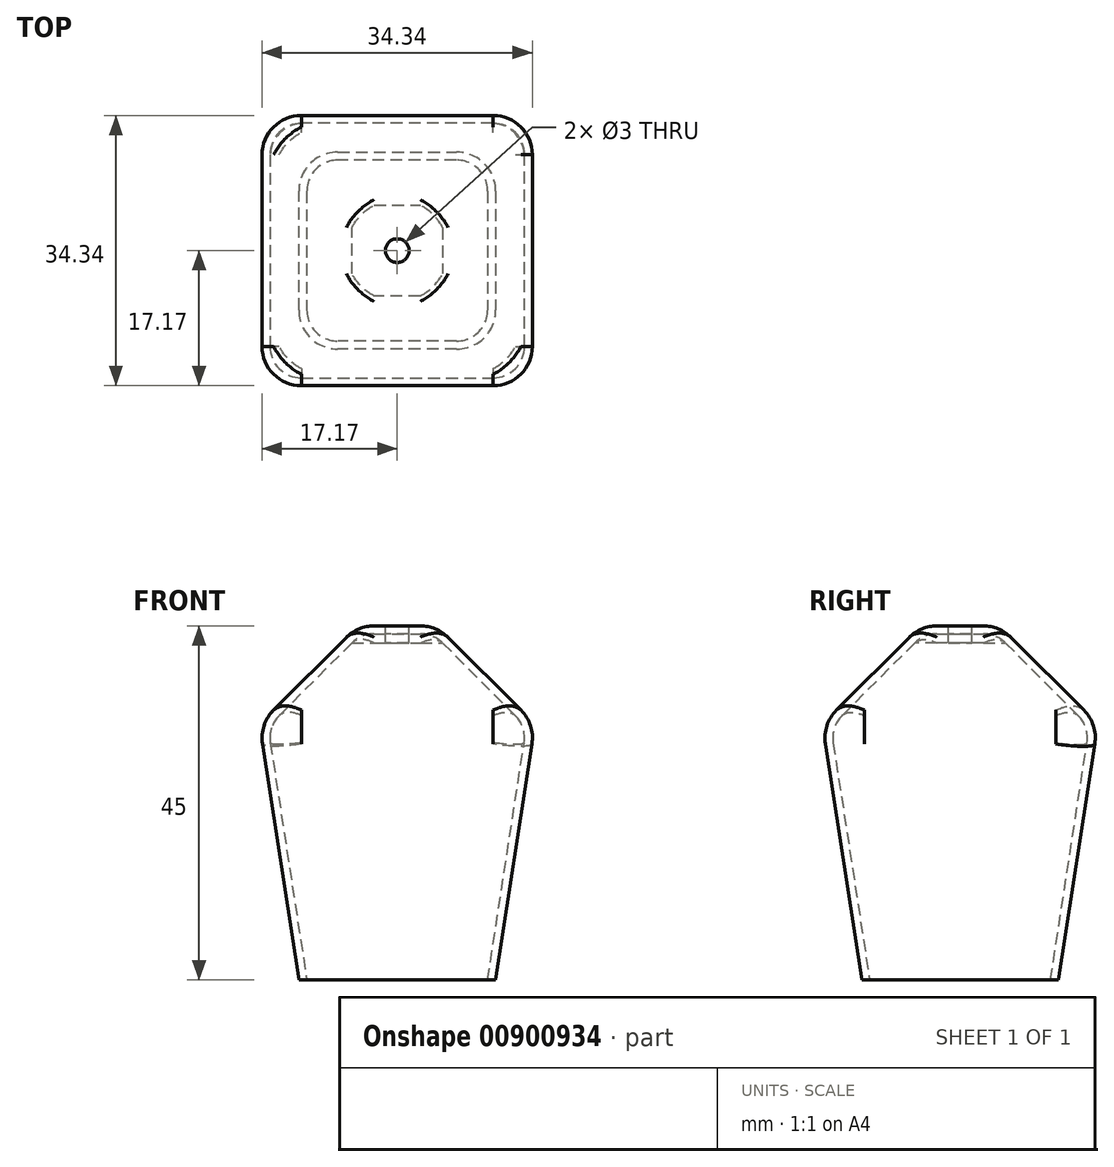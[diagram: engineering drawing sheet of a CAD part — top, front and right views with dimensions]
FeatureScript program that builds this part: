
annotation { "Feature Type Name" : "Feature", "Feature Type Description" : "" }
export const myFeature = defineFeature(function(context is Context, id is Id, definition is map)
    precondition{}
    {
        {
            var Q0;
            Q0=qCreatedBy(makeId("Top.planeOp"),FACE);
            var sketch = newSketch(context, id + "F0", { "sketchPlane" : qUnion([Q0])});
            skLineSegment(sketch, "E0.bottom", {"start": v(17.5, 17.5) * mm, "end": v(-17.5, 17.5) * mm});
            skLineSegment(sketch, "E0.top", {"start": v(17.5, -17.5) * mm, "end": v(-17.5, -17.5) * mm});
            skLineSegment(sketch, "E0.left", {"start": v(17.5, 17.5) * mm, "end": v(17.5, -17.5) * mm});
            skLineSegment(sketch, "E0.right", {"start": v(-17.5, 17.5) * mm, "end": v(-17.5, -17.5) * mm});
            skPoint(sketch, "E0.middle", {"position": v(0, 0) * mm});
            skSolve(sketch);
        }
        {
            var Q0;
            Q0 = qSketchRegion(id + "F0", true);
            extrude(context, id + "F1", {"entities" : qUnion([Q0]), "depth" : 45 * mm, "offsetDistance" : 25 * mm});
        }
        {
            var Q0;
            Q0=makeQuery(id+"F1.opExtrude","CAP_EDGE",EDGE,{"disambiguationData":[OSD([sQuery(id+"F0.wireOp",EDGE,"E0.left")])],"isStart":false});
            var Q1;
            Q1=makeQuery(id+"F1.opExtrude","CAP_EDGE",EDGE,{"disambiguationData":[OSD([sQuery(id+"F0.wireOp",EDGE,"E0.top")])],"isStart":false});
            var Q2;
            Q2=makeQuery(id+"F1.opExtrude","CAP_EDGE",EDGE,{"disambiguationData":[OSD([sQuery(id+"F0.wireOp",EDGE,"E0.right")])],"isStart":false});
            var Q3;
            Q3=makeQuery(id+"F1.opExtrude","CAP_EDGE",EDGE,{"disambiguationData":[OSD([sQuery(id+"F0.wireOp",EDGE,"E0.bottom")])],"isStart":false});
            chamfer(context, id + "F2", {"entities" : qUnion([Q0, Q1, Q2, Q3]), "width" : 12.5 * mm, "tangentPropagation" : true});
        }
        {
            var Q0;
            Q0=makeQuery(id+"F1.opExtrude","CAP_EDGE",EDGE,{"disambiguationData":[OSD([sQuery(id+"F0.wireOp",EDGE,"E0.left")])],"isStart":true});
            var Q1;
            Q1=makeQuery(id+"F1.opExtrude","CAP_EDGE",EDGE,{"disambiguationData":[OSD([sQuery(id+"F0.wireOp",EDGE,"E0.top")])],"isStart":true});
            var Q2;
            Q2=makeQuery(id+"F1.opExtrude","CAP_EDGE",EDGE,{"disambiguationData":[OSD([sQuery(id+"F0.wireOp",EDGE,"E0.right")])],"isStart":true});
            var Q3;
            Q3=makeQuery(id+"F1.opExtrude","CAP_EDGE",EDGE,{"disambiguationData":[OSD([sQuery(id+"F0.wireOp",EDGE,"E0.bottom")])],"isStart":true});
            chamfer(context, id + "F3", {"entities" : qUnion([Q0, Q1, Q2, Q3]), "chamferType" : ChamferType.TWO_OFFSETS, "width1" : 32.5 * mm, "oppositeDirection" : true, "width2" : 5 * mm, "tangentPropagation" : true});
        }
        {
            var Q0;
            {var subQ0=sQuery(id+"F0.wireOp",EDGE,"E0.top");Q0=makeQuery(id+"F2.opChamfer","BLEND_EDGE",EDGE,{"blendedFrom":[makeQuery(id+"F1.opExtrude","CAP_EDGE",EDGE,{"disambiguationData":[OSD([subQ0])],"isStart":false}),makeQuery(id+"F1.opExtrude","CAP_FACE",FACE,{"disambiguationData":[OSD([sQuery(id+"F0.wireOp",EDGE,"E0.bottom"),subQ0,sQuery(id+"F0.wireOp",EDGE,"E0.left"),sQuery(id+"F0.wireOp",EDGE,"E0.right")])],"isStart":false})],"blendedInto":[makeQuery(id+"F1.opExtrude","CAP_FACE",FACE,{"disambiguationData":[OSD([sQuery(id+"F0.wireOp",EDGE,"E0.bottom"),subQ0,sQuery(id+"F0.wireOp",EDGE,"E0.left"),sQuery(id+"F0.wireOp",EDGE,"E0.right")])],"isStart":false})]});}
            var Q1;
            {var subQ0=sQuery(id+"F0.wireOp",EDGE,"E0.left");Q1=makeQuery(id+"F2.opChamfer","BLEND_EDGE",EDGE,{"blendedFrom":[makeQuery(id+"F1.opExtrude","CAP_EDGE",EDGE,{"disambiguationData":[OSD([subQ0])],"isStart":false}),makeQuery(id+"F1.opExtrude","CAP_FACE",FACE,{"disambiguationData":[OSD([sQuery(id+"F0.wireOp",EDGE,"E0.bottom"),sQuery(id+"F0.wireOp",EDGE,"E0.top"),subQ0,sQuery(id+"F0.wireOp",EDGE,"E0.right")])],"isStart":false})],"blendedInto":[makeQuery(id+"F1.opExtrude","CAP_FACE",FACE,{"disambiguationData":[OSD([sQuery(id+"F0.wireOp",EDGE,"E0.bottom"),sQuery(id+"F0.wireOp",EDGE,"E0.top"),subQ0,sQuery(id+"F0.wireOp",EDGE,"E0.right")])],"isStart":false})]});}
            var Q2;
            {var subQ0=sQuery(id+"F0.wireOp",EDGE,"E0.bottom");Q2=makeQuery(id+"F2.opChamfer","BLEND_EDGE",EDGE,{"blendedFrom":[makeQuery(id+"F1.opExtrude","CAP_EDGE",EDGE,{"disambiguationData":[OSD([subQ0])],"isStart":false}),makeQuery(id+"F1.opExtrude","CAP_FACE",FACE,{"disambiguationData":[OSD([subQ0,sQuery(id+"F0.wireOp",EDGE,"E0.top"),sQuery(id+"F0.wireOp",EDGE,"E0.left"),sQuery(id+"F0.wireOp",EDGE,"E0.right")])],"isStart":false})],"blendedInto":[makeQuery(id+"F1.opExtrude","CAP_FACE",FACE,{"disambiguationData":[OSD([subQ0,sQuery(id+"F0.wireOp",EDGE,"E0.top"),sQuery(id+"F0.wireOp",EDGE,"E0.left"),sQuery(id+"F0.wireOp",EDGE,"E0.right")])],"isStart":false})]});}
            var Q3;
            {var subQ0=sQuery(id+"F0.wireOp",EDGE,"E0.right");Q3=makeQuery(id+"F2.opChamfer","BLEND_EDGE",EDGE,{"blendedFrom":[makeQuery(id+"F1.opExtrude","CAP_EDGE",EDGE,{"disambiguationData":[OSD([subQ0])],"isStart":false}),makeQuery(id+"F1.opExtrude","CAP_FACE",FACE,{"disambiguationData":[OSD([sQuery(id+"F0.wireOp",EDGE,"E0.bottom"),sQuery(id+"F0.wireOp",EDGE,"E0.top"),sQuery(id+"F0.wireOp",EDGE,"E0.left"),subQ0])],"isStart":false})],"blendedInto":[makeQuery(id+"F1.opExtrude","CAP_FACE",FACE,{"disambiguationData":[OSD([sQuery(id+"F0.wireOp",EDGE,"E0.bottom"),sQuery(id+"F0.wireOp",EDGE,"E0.top"),sQuery(id+"F0.wireOp",EDGE,"E0.left"),subQ0])],"isStart":false})]});}
            var Q4;
            Q4=makeQuery(id+"F2.opChamfer","BLEND_EDGE",EDGE,{"blendedFrom":[makeQuery(id+"F1.opExtrude","CAP_EDGE",EDGE,{"disambiguationData":[OSD([sQuery(id+"F0.wireOp",EDGE,"E0.top")])],"isStart":false}),makeQuery(id+"F1.opExtrude","CAP_EDGE",EDGE,{"disambiguationData":[OSD([sQuery(id+"F0.wireOp",EDGE,"E0.left")])],"isStart":false})],"blendedInto":[]});
            var Q5;
            Q5=makeQuery(id+"F2.opChamfer","BLEND_EDGE",EDGE,{"blendedFrom":[makeQuery(id+"F1.opExtrude","CAP_EDGE",EDGE,{"disambiguationData":[OSD([sQuery(id+"F0.wireOp",EDGE,"E0.top")])],"isStart":false}),makeQuery(id+"F1.opExtrude","CAP_EDGE",EDGE,{"disambiguationData":[OSD([sQuery(id+"F0.wireOp",EDGE,"E0.right")])],"isStart":false})],"blendedInto":[]});
            var Q6;
            Q6=makeQuery(id+"F2.opChamfer","BLEND_EDGE",EDGE,{"blendedFrom":[makeQuery(id+"F1.opExtrude","CAP_EDGE",EDGE,{"disambiguationData":[OSD([sQuery(id+"F0.wireOp",EDGE,"E0.bottom")])],"isStart":false}),makeQuery(id+"F1.opExtrude","CAP_EDGE",EDGE,{"disambiguationData":[OSD([sQuery(id+"F0.wireOp",EDGE,"E0.left")])],"isStart":false})],"blendedInto":[]});
            var Q7;
            Q7=makeQuery(id+"F2.opChamfer","BLEND_EDGE",EDGE,{"blendedFrom":[makeQuery(id+"F1.opExtrude","CAP_EDGE",EDGE,{"disambiguationData":[OSD([sQuery(id+"F0.wireOp",EDGE,"E0.bottom")])],"isStart":false}),makeQuery(id+"F1.opExtrude","CAP_EDGE",EDGE,{"disambiguationData":[OSD([sQuery(id+"F0.wireOp",EDGE,"E0.right")])],"isStart":false})],"blendedInto":[]});
            var Q8;
            {var subQ0=sQuery(id+"F0.wireOp",EDGE,"E0.top");Q8=makeQuery(id+"F3.opChamfer","BLEND_EDGE",EDGE,{"blendedFrom":[makeQuery(id+"F1.opExtrude","CAP_EDGE",EDGE,{"disambiguationData":[OSD([subQ0])],"isStart":true}),makeQuery(id+"F2.opChamfer","BLEND_FACE",FACE,{"disambiguationData":[OSD([subQ0])]})],"blendedInto":[makeQuery(id+"F2.opChamfer","BLEND_FACE",FACE,{"disambiguationData":[OSD([subQ0])]})]});}
            var Q9;
            {var subQ0=sQuery(id+"F0.wireOp",EDGE,"E0.right");Q9=makeQuery(id+"F3.opChamfer","BLEND_EDGE",EDGE,{"blendedFrom":[makeQuery(id+"F1.opExtrude","CAP_EDGE",EDGE,{"disambiguationData":[OSD([subQ0])],"isStart":true}),makeQuery(id+"F2.opChamfer","BLEND_FACE",FACE,{"disambiguationData":[OSD([subQ0])]})],"blendedInto":[makeQuery(id+"F2.opChamfer","BLEND_FACE",FACE,{"disambiguationData":[OSD([subQ0])]})]});}
            var Q10;
            {var subQ0=sQuery(id+"F0.wireOp",EDGE,"E0.bottom");Q10=makeQuery(id+"F3.opChamfer","BLEND_EDGE",EDGE,{"blendedFrom":[makeQuery(id+"F1.opExtrude","CAP_EDGE",EDGE,{"disambiguationData":[OSD([subQ0])],"isStart":true}),makeQuery(id+"F2.opChamfer","BLEND_FACE",FACE,{"disambiguationData":[OSD([subQ0])]})],"blendedInto":[makeQuery(id+"F2.opChamfer","BLEND_FACE",FACE,{"disambiguationData":[OSD([subQ0])]})]});}
            var Q11;
            {var subQ0=sQuery(id+"F0.wireOp",EDGE,"E0.left");Q11=makeQuery(id+"F3.opChamfer","BLEND_EDGE",EDGE,{"blendedFrom":[makeQuery(id+"F1.opExtrude","CAP_EDGE",EDGE,{"disambiguationData":[OSD([subQ0])],"isStart":true}),makeQuery(id+"F2.opChamfer","BLEND_FACE",FACE,{"disambiguationData":[OSD([subQ0])]})],"blendedInto":[makeQuery(id+"F2.opChamfer","BLEND_FACE",FACE,{"disambiguationData":[OSD([subQ0])]})]});}
            var Q12;
            Q12=makeQuery(id+"F3.opChamfer","BLEND_EDGE",EDGE,{"blendedFrom":[makeQuery(id+"F1.opExtrude","CAP_EDGE",EDGE,{"disambiguationData":[OSD([sQuery(id+"F0.wireOp",EDGE,"E0.bottom")])],"isStart":true}),makeQuery(id+"F1.opExtrude","CAP_EDGE",EDGE,{"disambiguationData":[OSD([sQuery(id+"F0.wireOp",EDGE,"E0.left")])],"isStart":true})],"blendedInto":[]});
            var Q13;
            Q13=makeQuery(id+"F3.opChamfer","BLEND_EDGE",EDGE,{"blendedFrom":[makeQuery(id+"F1.opExtrude","CAP_EDGE",EDGE,{"disambiguationData":[OSD([sQuery(id+"F0.wireOp",EDGE,"E0.top")])],"isStart":true}),makeQuery(id+"F1.opExtrude","CAP_EDGE",EDGE,{"disambiguationData":[OSD([sQuery(id+"F0.wireOp",EDGE,"E0.left")])],"isStart":true})],"blendedInto":[]});
            var Q14;
            Q14=makeQuery(id+"F3.opChamfer","BLEND_EDGE",EDGE,{"blendedFrom":[makeQuery(id+"F1.opExtrude","CAP_EDGE",EDGE,{"disambiguationData":[OSD([sQuery(id+"F0.wireOp",EDGE,"E0.top")])],"isStart":true}),makeQuery(id+"F1.opExtrude","CAP_EDGE",EDGE,{"disambiguationData":[OSD([sQuery(id+"F0.wireOp",EDGE,"E0.right")])],"isStart":true})],"blendedInto":[]});
            var Q15;
            Q15=makeQuery(id+"F3.opChamfer","BLEND_EDGE",EDGE,{"blendedFrom":[makeQuery(id+"F1.opExtrude","CAP_EDGE",EDGE,{"disambiguationData":[OSD([sQuery(id+"F0.wireOp",EDGE,"E0.bottom")])],"isStart":true}),makeQuery(id+"F1.opExtrude","CAP_EDGE",EDGE,{"disambiguationData":[OSD([sQuery(id+"F0.wireOp",EDGE,"E0.right")])],"isStart":true})],"blendedInto":[]});
            fillet(context, id + "F4", {"entities" : qUnion([Q0, Q1, Q2, Q3, Q4, Q5, Q6, Q7, Q8, Q9, Q10, Q11, Q12, Q13, Q14, Q15]), "radius" : 5 * mm, "tangentPropagation" : true, "allowEdgeOverflow" : false});
        }
        {
            var Q0;
            Q0=makeQuery(id+"F1.opExtrude","CAP_FACE",FACE,{"disambiguationData":[OSD([sQuery(id+"F0.wireOp",EDGE,"E0.bottom"),sQuery(id+"F0.wireOp",EDGE,"E0.top"),sQuery(id+"F0.wireOp",EDGE,"E0.left"),sQuery(id+"F0.wireOp",EDGE,"E0.right")])],"isStart":true});
            shell(context, id + "F5", {"entities" : qUnion([Q0]), "thickness" : 1 * mm});
        }
        {
            var Q0;
            {var subQ0=sQuery(id+"F0.wireOp",EDGE,"E0.left");var subQ1=sQuery(id+"F0.wireOp",EDGE,"E0.right");var subQ2=sQuery(id+"F0.wireOp",EDGE,"E0.top");var subQ3=sQuery(id+"F0.wireOp",EDGE,"E0.bottom");var subQ4=makeQuery(id+"F1.opExtrude","CAP_FACE",FACE,{"disambiguationData":[OSD([subQ3,subQ2,subQ0,subQ1])],"isStart":false});var subQ5=makeQuery(id+"F1.opExtrude","CAP_EDGE",EDGE,{"disambiguationData":[OSD([subQ0])],"isStart":false});var subQ6=makeQuery(id+"F1.opExtrude","CAP_EDGE",EDGE,{"disambiguationData":[OSD([subQ3])],"isStart":false});Q0=makeQuery(id+"F5.opShell","OFFSET_VERTEX",VERTEX,{"disambiguationData":[OSD([subQ3,subQ2,subQ0,subQ1]),TDD([makeQuery(id+"F4.opFillet","BLEND_VERTEX",VERTEX,{"blendedFrom":[makeQuery(id+"F2.opChamfer","BLEND_VERTEX",VERTEX,{"blendedFrom":[subQ6,subQ5,subQ4],"blendedInto":[subQ4]}),makeQuery(id+"F2.opChamfer","BLEND_EDGE",EDGE,{"blendedFrom":[subQ6,subQ5],"blendedInto":[]}),makeQuery(id+"F2.opChamfer","BLEND_EDGE",EDGE,{"blendedFrom":[subQ5,subQ4],"blendedInto":[subQ4]}),makeQuery(id+"F2.opChamfer","BLEND_FACE",FACE,{"disambiguationData":[OSD([subQ0])]})],"blendedInto":[makeQuery(id+"F2.opChamfer","BLEND_FACE",FACE,{"disambiguationData":[OSD([subQ0])]})]})])]});}
            var Q1;
            {var subQ0=sQuery(id+"F0.wireOp",EDGE,"E0.bottom");var subQ1=sQuery(id+"F0.wireOp",EDGE,"E0.right");var subQ2=sQuery(id+"F0.wireOp",EDGE,"E0.left");var subQ3=sQuery(id+"F0.wireOp",EDGE,"E0.top");var subQ4=makeQuery(id+"F1.opExtrude","CAP_FACE",FACE,{"disambiguationData":[OSD([subQ0,subQ3,subQ2,subQ1])],"isStart":false});var subQ5=makeQuery(id+"F1.opExtrude","CAP_EDGE",EDGE,{"disambiguationData":[OSD([subQ0])],"isStart":false});var subQ6=makeQuery(id+"F1.opExtrude","CAP_EDGE",EDGE,{"disambiguationData":[OSD([subQ2])],"isStart":false});Q1=makeQuery(id+"F5.opShell","OFFSET_VERTEX",VERTEX,{"disambiguationData":[OSD([subQ0,subQ3,subQ2,subQ1]),TDD([makeQuery(id+"F4.opFillet","BLEND_VERTEX",VERTEX,{"blendedFrom":[makeQuery(id+"F2.opChamfer","BLEND_VERTEX",VERTEX,{"blendedFrom":[subQ5,subQ6,subQ4],"blendedInto":[subQ4]}),makeQuery(id+"F2.opChamfer","BLEND_EDGE",EDGE,{"blendedFrom":[subQ5,subQ6],"blendedInto":[]}),makeQuery(id+"F2.opChamfer","BLEND_EDGE",EDGE,{"blendedFrom":[subQ5,subQ4],"blendedInto":[subQ4]}),makeQuery(id+"F2.opChamfer","BLEND_FACE",FACE,{"disambiguationData":[OSD([subQ0])]})],"blendedInto":[makeQuery(id+"F2.opChamfer","BLEND_FACE",FACE,{"disambiguationData":[OSD([subQ0])]})]})])]});}
            var Q2;
            {var subQ0=sQuery(id+"F0.wireOp",EDGE,"E0.bottom");var subQ1=sQuery(id+"F0.wireOp",EDGE,"E0.right");var subQ2=sQuery(id+"F0.wireOp",EDGE,"E0.left");var subQ3=sQuery(id+"F0.wireOp",EDGE,"E0.top");var subQ4=makeQuery(id+"F1.opExtrude","CAP_FACE",FACE,{"disambiguationData":[OSD([subQ0,subQ3,subQ2,subQ1])],"isStart":false});var subQ5=makeQuery(id+"F1.opExtrude","CAP_EDGE",EDGE,{"disambiguationData":[OSD([subQ0])],"isStart":false});var subQ6=makeQuery(id+"F1.opExtrude","CAP_EDGE",EDGE,{"disambiguationData":[OSD([subQ1])],"isStart":false});Q2=makeQuery(id+"F5.opShell","OFFSET_VERTEX",VERTEX,{"disambiguationData":[OSD([subQ0,subQ3,subQ2,subQ1]),TDD([makeQuery(id+"F4.opFillet","BLEND_VERTEX",VERTEX,{"blendedFrom":[makeQuery(id+"F2.opChamfer","BLEND_VERTEX",VERTEX,{"blendedFrom":[subQ5,subQ6,subQ4],"blendedInto":[subQ4]}),makeQuery(id+"F2.opChamfer","BLEND_EDGE",EDGE,{"blendedFrom":[subQ5,subQ6],"blendedInto":[]}),makeQuery(id+"F2.opChamfer","BLEND_EDGE",EDGE,{"blendedFrom":[subQ5,subQ4],"blendedInto":[subQ4]}),makeQuery(id+"F2.opChamfer","BLEND_FACE",FACE,{"disambiguationData":[OSD([subQ0])]})],"blendedInto":[makeQuery(id+"F2.opChamfer","BLEND_FACE",FACE,{"disambiguationData":[OSD([subQ0])]})]})])]});}
            cPlane(context, id + "F6", {"entities" : qUnion([Q0, Q1, Q2]), "cplaneType" : CPlaneType.THREE_POINT, "offset" : 25 * mm, "width" : 150 * mm, "height" : 150 * mm});
        }
        {
            var Q0;
            Q0=qCreatedBy(id+"F6.planeOp",FACE);
            var sketch = newSketch(context, id + "F7", { "sketchPlane" : qUnion([Q0])});
            skLineSegment(sketch, "E1.0", {"start": v(-2.93, -5.76) * mm, "end": v(2.93, -5.76) * mm});
            skEllipticalArc(sketch, "E2.0", {});
            skLineSegment(sketch, "E3.0", {"start": v(-5.76, 2.93) * mm, "end": v(-5.76, -2.93) * mm});
            skEllipticalArc(sketch, "E4.0", {});
            skLineSegment(sketch, "E5.0", {"start": v(2.93, 5.76) * mm, "end": v(-2.93, 5.76) * mm});
            skEllipticalArc(sketch, "E6.0", {});
            skLineSegment(sketch, "E7.0", {"start": v(5.76, -2.93) * mm, "end": v(5.76, 2.93) * mm});
            skEllipticalArc(sketch, "E8.0", {});
            const initialGuessF7  = {"E2.0": [-0.002928932188134527, -0.002928932188134629, -0.7071067811865467, 0.7071067811865483, 0.004, 0.0023094010767585097, 1.0471975511966014, 2.0943951023931966], "E4.0": [-0.002928932188134532, 0.002928932188134436, 0.7071067811865482, 0.7071067811865468, 0.004, 0.002309401076758497, 1.047197551196599, 2.0943951023931975], "E6.0": [0.002928932188134531, 0.002928932188134432, 0.7071067811865485, -0.7071067811865466, 0.004, 0.002309401076758498, 1.0471975511965952, 2.0943951023931935], "E8.0": [0.002928932188134531, -0.002928932188134627, -0.7071067811865465, -0.7071067811865485, 0.004, 0.0023094010767585084, 1.0471975511965965, 2.0943951023931944]};
            skSetInitialGuess(sketch, initialGuessF7);
            skSolve(sketch);
        }
        {
            var Q0;
            Q0 = qSketchRegion(id + "F7", true);
            var Q1;
            Q1=makeQuery(id+"F1.opExtrude","SWEPT_BODY",BODY,{"disambiguationData":[OSD([sQuery(id+"F0.wireOp",EDGE,"E0.bottom"),sQuery(id+"F0.wireOp",EDGE,"E0.top"),sQuery(id+"F0.wireOp",EDGE,"E0.left"),sQuery(id+"F0.wireOp",EDGE,"E0.right")])]});
            extrude(context, id + "F8", {"entities" : qUnion([Q0]), "endBound" : BoundingType.UP_TO_BODY, "oppositeDirection" : true, "depth" : 25 * mm, "endBoundEntityBody" : qUnion([Q1]), "offsetDistance" : 25 * mm});
        }
        {
            var Q0;
            Q0=makeQuery(id+"F1.opExtrude","CAP_FACE",FACE,{"disambiguationData":[OSD([sQuery(id+"F0.wireOp",EDGE,"E0.bottom"),sQuery(id+"F0.wireOp",EDGE,"E0.top"),sQuery(id+"F0.wireOp",EDGE,"E0.left"),sQuery(id+"F0.wireOp",EDGE,"E0.right")])],"isStart":false});
            var sketch = newSketch(context, id + "F9", { "sketchPlane" : qUnion([Q0])});
            skCircle(sketch, "E9", {"center": v(0, 0) * mm, "radius": 1.5 * mm});
            skSolve(sketch);
        }
        {
            var Q0;
            Q0 = qSketchRegion(id + "F9", true);
            extrude(context, id + "F10", {"entities" : qUnion([Q0]), "operationType" : NewBodyOperationType.REMOVE, "endBound" : BoundingType.THROUGH_ALL, "oppositeDirection" : true, "depth" : 25 * mm, "offsetDistance" : 25 * mm});
        }
    });
